# Revit family: Toilet-Wall_Mount-KOHLER-Grande-K-22638A.rfa_
name_source: partatom
category: Plumbing Fixtures
units: mm (PartAtom-declared; Revit-internal decimal feet)

## family parameters
Cut with Voids When Loaded = No
Host = Face
OmniClass Number = 23.31.19.00
OmniClass Title = Toilets
Part Type = Normal
Room Calculation Point = No
Round Connector Dimension = Use Diameter
Shared = No

## types (3) — shared parameters
ADA Compliant = No
Assembly Code = D2010100
CW Connection = Yes
Cold Water Inlet = Cold Water Inlet
Date Modified = 12/06/2022
Default Elevation = 0"
Finish = Kohler-Vitreous_China-0-White
Flow Rate = 0 GPM
Flush Rate- GPF = GPF
Flush Rate- LPF = LPF
HW Connection = No
Hot Water Inlet = Hot Water Inlet
Length = 22 1/16"
Manufacturer = Kohler Co.
Master Format 2014 = 22 42 13.13
Master Format 2014 Name = Residential Water Closets
Material = Vitreous China
Pressure = 0.00 psi
Product Name = Grande
Seat Included = Yes
URL = https://www.kohlerasiapacific.com
Vent Connection = No
Waste Connection = Yes
Waste Water Outlet = Waste Water Outlet
WaterSense Certified = No

## per-type parameters (varying)
| type | Description | Elite Sea | Height | Model | Type | Width | Wrap Ove |
| Wrap Ove,0-White | Wall Hung Toilet Pan And Wrap Ove | No | 15 1/2" | K-22638A-0 | 1 | 14 7/8" | Yes |
| Elite Sea,0-White | Wall Hung Toilet Pan And Elite Sea | Yes | 15 5/16" | K-22638A-ELS-0 | 2 | 14 5/8" | No |
| Slim Sea,0-White | Wall Hung Toilet Pan And Slim Sea | Yes | 15 5/16" | K-22638A-SLS-0 | 3 | 14 5/8" | No |

## geometry (parser evidence)
native form markers: Sweep x5
no freeform markers — native parametric forms only
